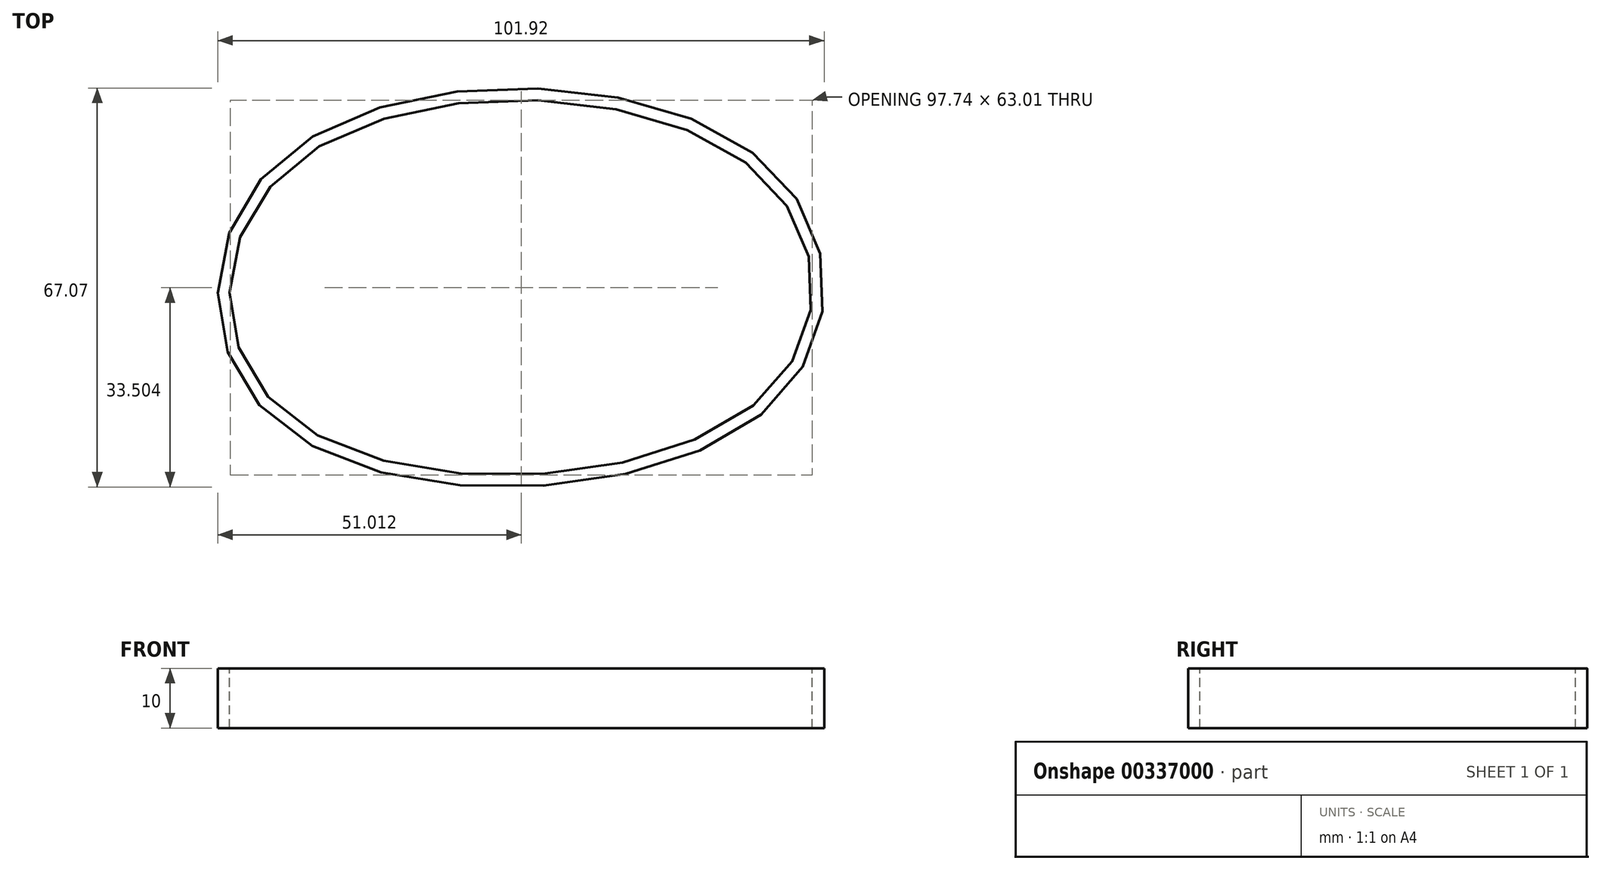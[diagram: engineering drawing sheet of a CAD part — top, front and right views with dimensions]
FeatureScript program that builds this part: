
annotation { "Feature Type Name" : "Feature", "Feature Type Description" : "" }
export const myFeature = defineFeature(function(context is Context, id is Id, definition is map)
    precondition{}
    {
        {
            var Q0;
            Q0=qCreatedBy(makeId("Top.planeOp"),FACE);
            var sketch = newSketch(context, id + "F0", { "sketchPlane" : qUnion([Q0])});
            skFitSpline(sketch, "E0", {"points": [v(-41.57, 23.93) * mm, v(35.8, 23.94) * mm, v(37.55, -14.92) * mm, v(-42.26, -17.6) * mm, v(-41.57, 23.93) * mm]});
            skSolve(sketch);
        }
        {
            var Q0;
            Q0=qCreatedBy(makeId("Right.planeOp"),FACE);
            var sketch = newSketch(context, id + "F1", { "sketchPlane" : qUnion([Q0])});
            skLineSegment(sketch, "E1.0", {"start": v(-27.8, 0) * mm, "end": v(35.15, 0) * mm});
            skLineSegment(sketch, "E2.bottom", {"start": v(35.15, 0) * mm, "end": v(37.15, 0) * mm});
            skLineSegment(sketch, "E2.top", {"start": v(35.15, 10) * mm, "end": v(37.15, 10) * mm});
            skLineSegment(sketch, "E2.left", {"start": v(35.15, 0) * mm, "end": v(35.15, 10) * mm});
            skLineSegment(sketch, "E2.right", {"start": v(37.15, 0) * mm, "end": v(37.15, 10) * mm});
            skSolve(sketch);
        }
        {
            var Q0;
            Q0=makeQuery(id+"F1.imprint","IMPRINT",FACE,{"disambiguationData":[TD([[makeQuery(id+"F1.imprint","IMPRINT",EDGE,{"derivedFrom":sQuery(id+"F1.wireOp",EDGE,"E2.bottom")}),1.0]])]});
            var Q1;
            Q1=sQuery(id+"F0.wireOp",EDGE,"E0");
            sweep(context, id + "F2", {"profiles" : qUnion([Q0]), "path" : qUnion([Q1])});
        }
    });
